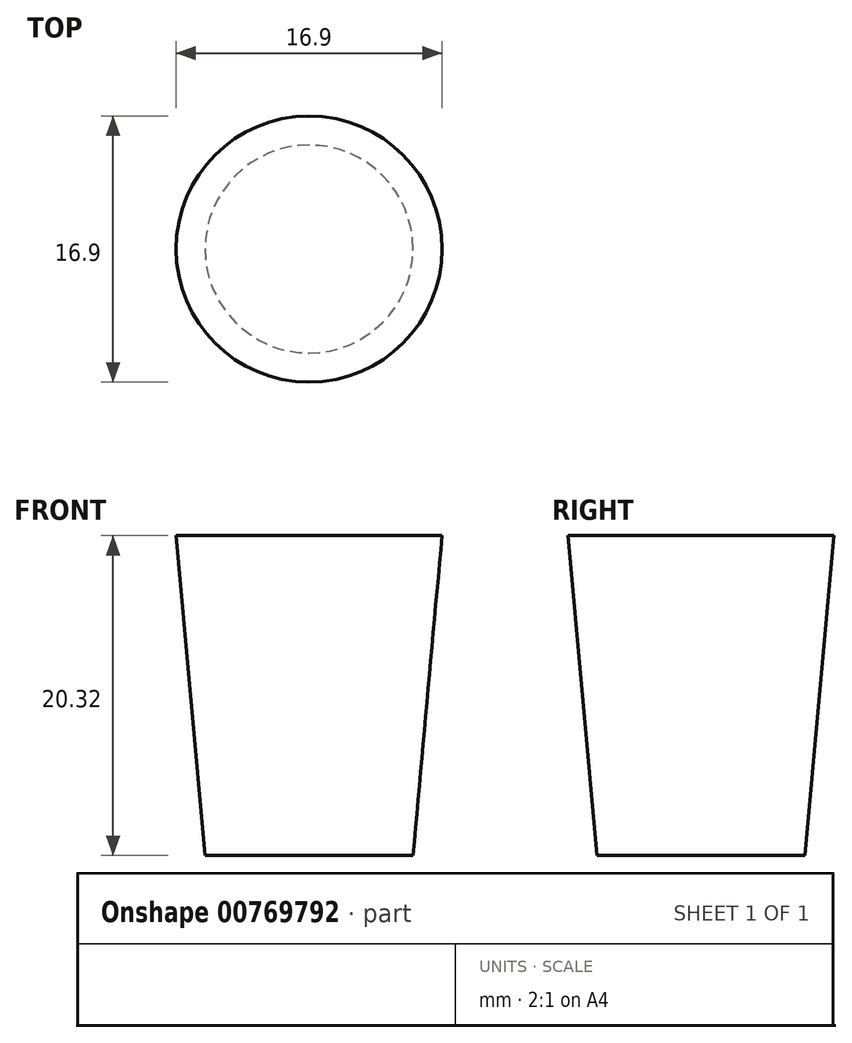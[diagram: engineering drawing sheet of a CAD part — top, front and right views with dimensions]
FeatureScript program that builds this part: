
annotation { "Feature Type Name" : "Feature", "Feature Type Description" : "" }
export const myFeature = defineFeature(function(context is Context, id is Id, definition is map)
    precondition{}
    {
        {
            var Q0;
            Q0=qCreatedBy(makeId("Top.planeOp"),FACE);
            var sketch = newSketch(context, id + "F0", { "sketchPlane" : qUnion([Q0])});
            skCircle(sketch, "E0", {"center": v(0, 0) * mm, "radius": 6.6 * mm});
            skSolve(sketch);
        }
        {
            var Q0;
            Q0=makeQuery(id+"F0.imprint","IMPRINT",FACE,{"disambiguationData":[TD([[makeQuery(id+"F0.imprint","IMPRINT",EDGE,{"derivedFrom":sQuery(id+"F0.wireOp",EDGE,"E0")}),1.0]])]});
            cPlane(context, id + "F1", {"entities" : qUnion([Q0]), "cplaneType" : CPlaneType.OFFSET, "offset" : 20.32 * mm, "width" : 152.4 * mm, "height" : 152.4 * mm});
        }
        {
            var Q0;
            Q0=qCreatedBy(id+"F1.planeOp",FACE);
            var sketch = newSketch(context, id + "F2", { "sketchPlane" : qUnion([Q0])});
            skCircle(sketch, "E1", {"center": v(0, 0) * mm, "radius": 8.45 * mm});
            skSolve(sketch);
        }
        {
            var Q0;
            Q0=makeQuery(id+"F0.imprint","IMPRINT",FACE,{"disambiguationData":[TD([[makeQuery(id+"F0.imprint","IMPRINT",EDGE,{"derivedFrom":sQuery(id+"F0.wireOp",EDGE,"E0")}),1.0]])]});
            var Q1;
            Q1=makeQuery(id+"F2.imprint","IMPRINT",FACE,{"disambiguationData":[TD([[makeQuery(id+"F2.imprint","IMPRINT",EDGE,{"derivedFrom":sQuery(id+"F2.wireOp",EDGE,"E1")}),1.0]])]});
            loft(context, id + "F3", {"sheetProfilesArray" : [{ "sheetProfileEntities" : qUnion([Q0]) }, { "sheetProfileEntities" : qUnion([Q1]) }]});
        }
    });
